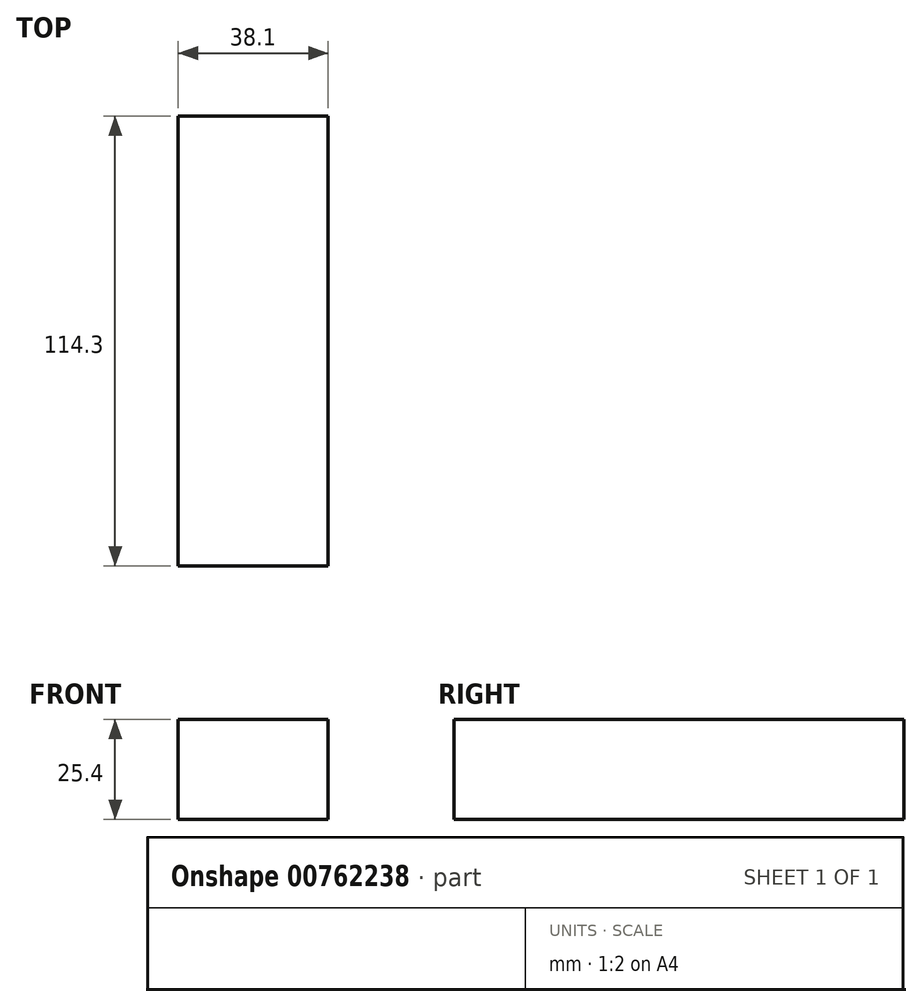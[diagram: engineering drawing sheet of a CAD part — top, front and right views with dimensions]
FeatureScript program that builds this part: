
annotation { "Feature Type Name" : "Feature", "Feature Type Description" : "" }
export const myFeature = defineFeature(function(context is Context, id is Id, definition is map)
    precondition{}
    {
        {
            var Q0;
            Q0=qCreatedBy(makeId("Top.planeOp"),FACE);
            var sketch = newSketch(context, id + "F0", { "sketchPlane" : qUnion([Q0])});
            skLineSegment(sketch, "E0.bottom", {"start": v(0, 0) * mm, "end": v(38.1, 0) * mm});
            skLineSegment(sketch, "E0.top", {"start": v(0, 114.3) * mm, "end": v(38.1, 114.3) * mm});
            skLineSegment(sketch, "E0.left", {"start": v(0, 0) * mm, "end": v(0, 114.3) * mm});
            skLineSegment(sketch, "E0.right", {"start": v(38.1, 0) * mm, "end": v(38.1, 114.3) * mm});
            skSolve(sketch);
        }
        {
            var Q0;
            Q0 = qSketchRegion(id + "F0", true);
            extrude(context, id + "F1", {"entities" : qUnion([Q0]), "depth" : 25.4 * mm, "offsetDistance" : 25.4 * mm});
        }
    });
